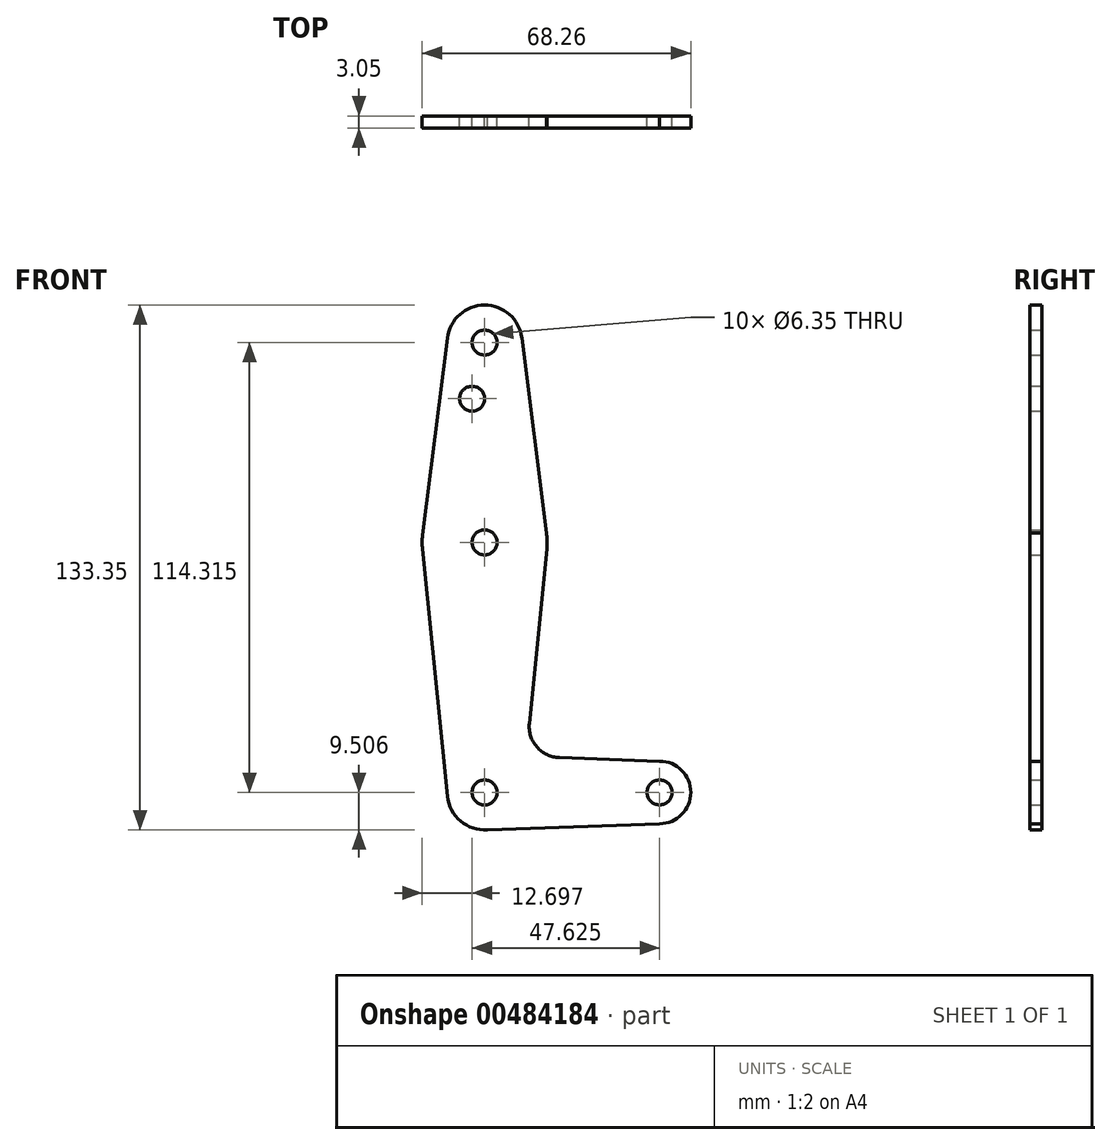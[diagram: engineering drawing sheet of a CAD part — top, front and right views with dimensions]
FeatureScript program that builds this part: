
annotation { "Feature Type Name" : "Feature", "Feature Type Description" : "" }
export const myFeature = defineFeature(function(context is Context, id is Id, definition is map)
    precondition{}
    {
        {
            var Q0;
            Q0=qCreatedBy(makeId("Front.planeOp"),FACE);
            var sketch = newSketch(context, id + "F0", { "sketchPlane" : qUnion([Q0])});
            skLineSegment(sketch, "E0", {"start": v(-98.22, 65.26) * mm, "end": v(-98.22, -49.04) * mm, "construction": true});
            skCircle(sketch, "E1", {"center": v(-98.22, 65.26) * mm, "radius": 9.53 * mm});
            skCircle(sketch, "E2", {"center": v(-98.22, 14.46) * mm, "radius": 15.88 * mm});
            skCircle(sketch, "E3", {"center": v(-98.22, -49.04) * mm, "radius": 9.53 * mm});
            skLineSegment(sketch, "E4", {"start": v(-98.22, -49.04) * mm, "end": v(-53.77, -49.04) * mm, "construction": true});
            skCircle(sketch, "E5", {"center": v(-53.77, -49.04) * mm, "radius": 7.94 * mm});
            skLineSegment(sketch, "E6", {"start": v(-114.01, 12.87) * mm, "end": v(-107.7, -50) * mm});
            skLineSegment(sketch, "E7", {"start": v(-86.88, -31.45) * mm, "end": v(-82.42, 12.87) * mm});
            skLineSegment(sketch, "E8", {"start": v(-82.42, 16.05) * mm, "end": v(-88.77, 66.45) * mm});
            skLineSegment(sketch, "E9", {"start": v(-113.97, 16.42) * mm, "end": v(-107.67, 66.45) * mm});
            skCircle(sketch, "E10", {"center": v(-98.22, 65.26) * mm, "radius": 3.18 * mm});
            skCircle(sketch, "E11", {"center": v(-98.22, -49.05) * mm, "radius": 3.18 * mm});
            skCircle(sketch, "E12", {"center": v(-53.77, -49.04) * mm, "radius": 3.18 * mm});
            skCircle(sketch, "E13", {"center": v(-98.24, 14.5) * mm, "radius": 3.18 * mm});
            skCircle(sketch, "E14", {"center": v(-101.4, 50.99) * mm, "radius": 3.18 * mm});
            skLineSegment(sketch, "E15", {"start": v(-79.25, -40.2) * mm, "end": v(-53.77, -41.1) * mm});
            skLineSegment(sketch, "E16", {"start": v(-53.77, -56.98) * mm, "end": v(-98.22, -58.56) * mm});
            skPoint(sketch, "E17.newPointB", {"position": v(-88.74, -50) * mm});
            skArc(sketch, "E17.filletArc", {"start": v(-86.88, -31.45) * mm, "mid": v(-84.96, -37.47) * mm, "end": v(-79.25, -40.2) * mm});
            skSolve(sketch);
        }
        {
            var Q0;
            Q0 = qSketchRegion(id + "F0", true);
            extrude(context, id + "F1", {"entities" : qUnion([Q0]), "depth" : 3.05 * mm});
        }
        {
            var Q0;
            Q0 = qSketchRegion(id + "F0", true);
            extrude(context, id + "F2", {"entities" : qUnion([Q0]), "depth" : 3.05 * mm});
        }
    });
